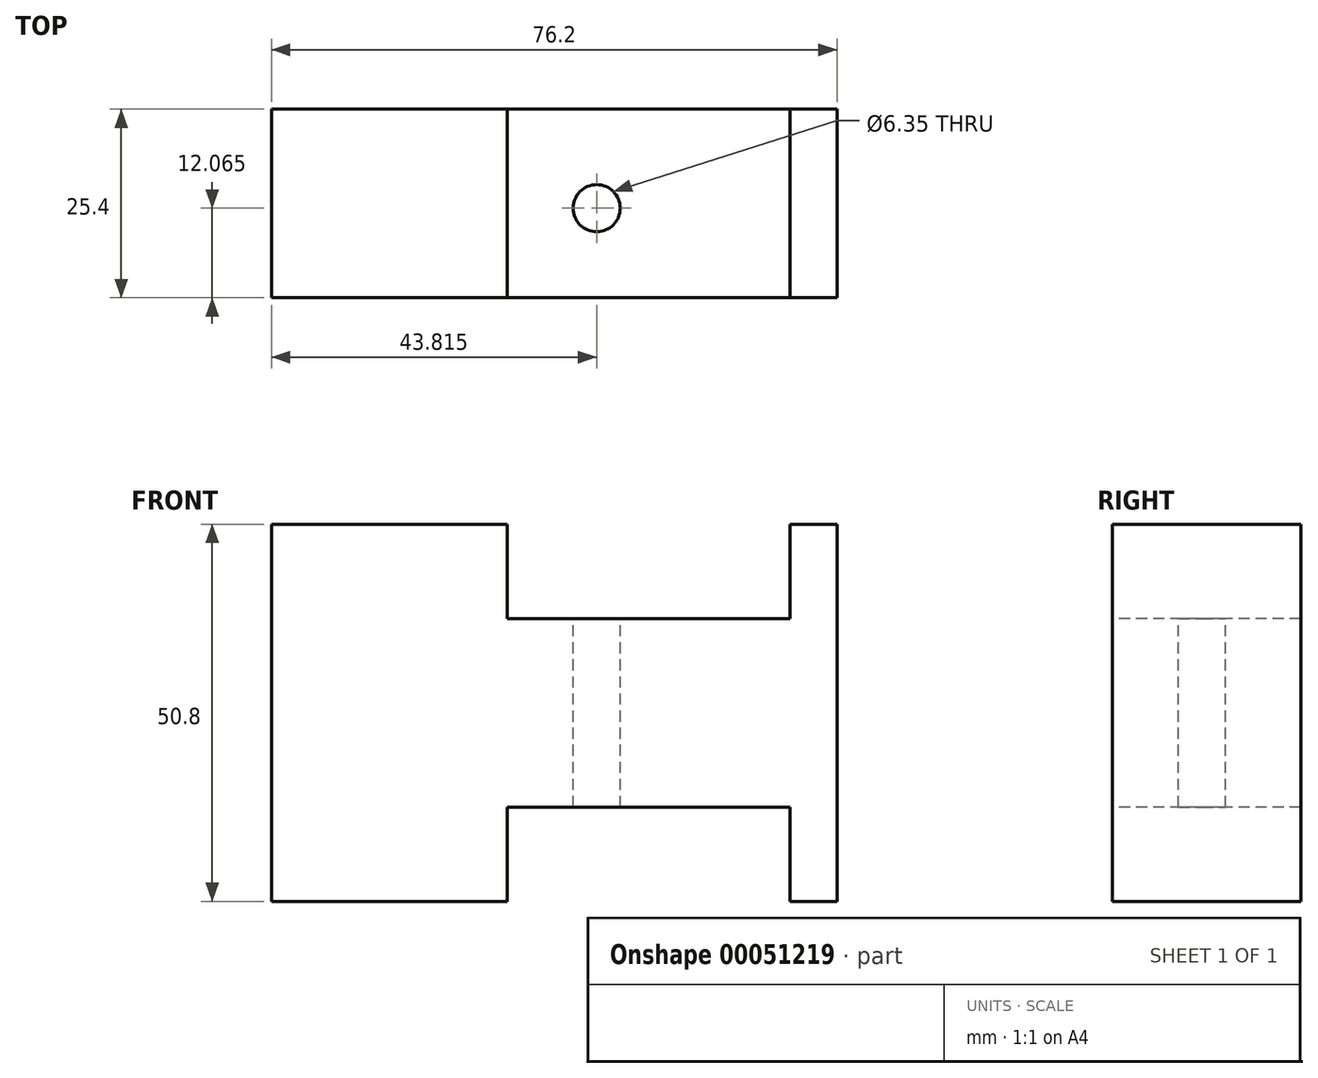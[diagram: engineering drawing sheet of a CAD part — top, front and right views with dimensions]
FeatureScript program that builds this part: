
annotation { "Feature Type Name" : "Feature", "Feature Type Description" : "" }
export const myFeature = defineFeature(function(context is Context, id is Id, definition is map)
    precondition{}
    {
        {
            var Q0;
            Q0=qCreatedBy(makeId("Front.planeOp"),FACE);
            var sketch = newSketch(context, id + "F0", { "sketchPlane" : qUnion([Q0])});
            skLineSegment(sketch, "E0.bottom", {"start": v(0, 0) * mm, "end": v(76.2, 0) * mm});
            skLineSegment(sketch, "E0.top", {"start": v(0, 25.4) * mm, "end": v(76.2, 25.4) * mm});
            skLineSegment(sketch, "E0.left", {"start": v(0, 0) * mm, "end": v(0, 25.4) * mm});
            skLineSegment(sketch, "E0.right", {"start": v(76.2, 0) * mm, "end": v(76.2, 25.4) * mm});
            skSolve(sketch);
        }
        {
            var Q0;
            Q0=qSketchRegion(id+"F0",true);
            extrude(context, id + "F1", {"entities" : qUnion([Q0]), "depth" : 25.4 * mm});
        }
        {
            var Q0;
            Q0=makeQuery(id+"F1.opExtrude","SWEPT_FACE",FACE,{"disambiguationData":[OSD([sQuery(id+"F0.wireOp",EDGE,"E0.top")])]});
            var sketch = newSketch(context, id + "F2", { "sketchPlane" : qUnion([Q0])});
            skLineSegment(sketch, "E1.bottom", {"start": v(69.85, 0) * mm, "end": v(31.75, 0) * mm});
            skLineSegment(sketch, "E1.top", {"start": v(69.85, -25.4) * mm, "end": v(31.75, -25.4) * mm});
            skLineSegment(sketch, "E1.left", {"start": v(69.85, 0) * mm, "end": v(69.85, -25.4) * mm});
            skLineSegment(sketch, "E1.right", {"start": v(31.75, 0) * mm, "end": v(31.75, -25.4) * mm});
            skSolve(sketch);
        }
        {
            var Q0;
            Q0=makeQuery(id+"F2.imprint","IMPRINT",FACE,{"disambiguationData":[TD([[makeQuery(id+"F2.imprint","IMPRINT",EDGE,{"derivedFrom":sQuery(id+"F2.wireOp",EDGE,"E1.bottom")}),-1.0]])]});
            extrude(context, id + "F3", {"entities" : qUnion([Q0]), "operationType" : NewBodyOperationType.REMOVE, "oppositeDirection" : true, "depth" : 12.7 * mm});
        }
        {
            var Q0;
            Q0=makeQuery(id+"F3.boolean.opBoolean","COPY",FACE,{"derivedFrom":makeQuery(id+"F3.opExtrude","CAP_FACE",FACE,{"disambiguationData":[OSD([sQuery(id+"F2.wireOp",EDGE,"E1.bottom"),sQuery(id+"F2.wireOp",EDGE,"E1.top"),sQuery(id+"F2.wireOp",EDGE,"E1.left"),sQuery(id+"F2.wireOp",EDGE,"E1.right")])],"isStart":false})});
            var sketch = newSketch(context, id + "F4", { "sketchPlane" : qUnion([Q0])});
            skCircle(sketch, "E2", {"center": v(43.81, -13.34) * mm, "radius": 3.18 * mm});
            skSolve(sketch);
        }
        {
            var Q0;
            Q0=qSketchRegion(id+"F4",true);
            extrude(context, id + "F5", {"entities" : qUnion([Q0]), "operationType" : NewBodyOperationType.REMOVE, "oppositeDirection" : true, "depth" : 12.7 * mm});
        }
        {
            var Q0;
            Q0=makeQuery(id+"F1.opExtrude","SWEPT_BODY",BODY,{"disambiguationData":[OSD([sQuery(id+"F0.wireOp",EDGE,"E0.bottom"),sQuery(id+"F0.wireOp",EDGE,"E0.top"),sQuery(id+"F0.wireOp",EDGE,"E0.left"),sQuery(id+"F0.wireOp",EDGE,"E0.right")])]});
            var Q1;
            Q1=qCreatedBy(makeId("Top.planeOp"),FACE);
            mirror(context, id + "F6", {"operationType" : NewBodyOperationType.ADD, "entities" : qUnion([Q0]), "mirrorPlane" : qUnion([Q1])});
        }
    });
